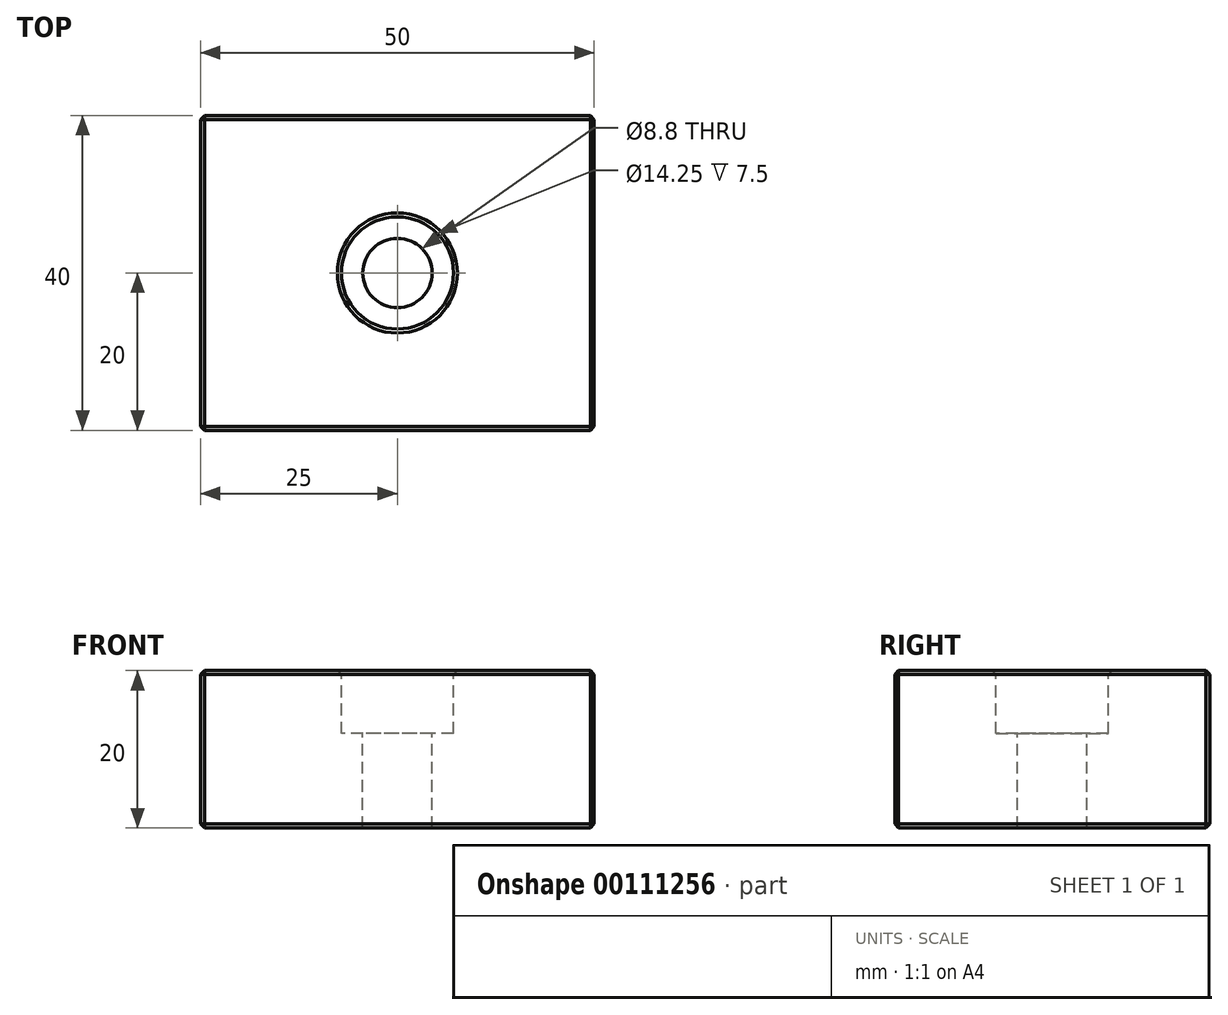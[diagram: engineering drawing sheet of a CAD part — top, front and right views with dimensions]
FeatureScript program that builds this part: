
annotation { "Feature Type Name" : "Feature", "Feature Type Description" : "" }
export const myFeature = defineFeature(function(context is Context, id is Id, definition is map)
    precondition{}
    {
        {
            var Q0;
            Q0=qCreatedBy(makeId("Top.planeOp"),FACE);
            var sketch = newSketch(context, id + "F0", { "sketchPlane" : qUnion([Q0])});
            skLineSegment(sketch, "E0.bottom", {"start": v(25, 20) * mm, "end": v(-25, 20) * mm});
            skLineSegment(sketch, "E0.top", {"start": v(25, -20) * mm, "end": v(-25, -20) * mm});
            skLineSegment(sketch, "E0.left", {"start": v(25, 20) * mm, "end": v(25, -20) * mm});
            skLineSegment(sketch, "E0.right", {"start": v(-25, 20) * mm, "end": v(-25, -20) * mm});
            skPoint(sketch, "E0.middle", {"position": v(0, 0) * mm});
            skSolve(sketch);
        }
        {
            var Q0;
            Q0=makeQuery(id+"F0.imprint","IMPRINT",FACE,{"disambiguationData":[TD([[makeQuery(id+"F0.imprint","IMPRINT",EDGE,{"derivedFrom":sQuery(id+"F0.wireOp",EDGE,"E0.bottom")}),1.0]])]});
            extrude(context, id + "F1", {"entities" : qUnion([Q0]), "depth" : 20 * mm});
        }
        {
            var Q0;
            Q0=makeQuery(id+"F1.opExtrude","CAP_FACE",FACE,{"disambiguationData":[OSD([sQuery(id+"F0.wireOp",EDGE,"E0.bottom"),sQuery(id+"F0.wireOp",EDGE,"E0.top"),sQuery(id+"F0.wireOp",EDGE,"E0.left"),sQuery(id+"F0.wireOp",EDGE,"E0.right")])],"isStart":false});
            var sketch = newSketch(context, id + "F2", { "sketchPlane" : qUnion([Q0])});
            skLineSegment(sketch, "E1", {"start": v(-25, 0) * mm, "end": v(25, 0) * mm});
            skPoint(sketch, "E2", {"position": v(0, 0) * mm});
            skSolve(sketch);
        }
        {
            var Q0;
            Q0=sQuery(id+"F2.wireOp",VERTEX,"E2");
            var Q1;
            Q1=makeQuery(id+"F1.opExtrude","SWEPT_BODY",BODY,{"disambiguationData":[OSD([sQuery(id+"F0.wireOp",EDGE,"E0.bottom"),sQuery(id+"F0.wireOp",EDGE,"E0.top"),sQuery(id+"F0.wireOp",EDGE,"E0.left"),sQuery(id+"F0.wireOp",EDGE,"E0.right")])]});
            hole(context, id + "F3", {"style" : HoleStyle.C_BORE, "endStyle" : HoleEndStyle.THROUGH, "standardTappedOrClearance" : lookupTablePath({ "standard" : "ISO", "fit" : "Normal", "size" : "M8", "type" : "Clearance" }), "standardBlindInLast" : lookupTablePath({ "fit" : "Standard", "standard" : "ISO", "size" : "M8", "type" : "Clearance" }), "holeDiameter" : 8.8 * mm, "cBoreDiameter" : 14.25 * mm, "cBoreDepth" : 8 * mm, "locations" : qUnion([Q0]), "scope" : qUnion([Q1]), "isTappedThrough" : true});
        }
        {
            var Q0;
            Q0=makeQuery(id+"F1.opExtrude","CAP_FACE",FACE,{"disambiguationData":[OSD([sQuery(id+"F0.wireOp",EDGE,"E0.bottom"),sQuery(id+"F0.wireOp",EDGE,"E0.top"),sQuery(id+"F0.wireOp",EDGE,"E0.left"),sQuery(id+"F0.wireOp",EDGE,"E0.right")])],"isStart":false});
            var Q1;
            Q1=makeQuery(id+"F1.opExtrude","SWEPT_FACE",FACE,{"disambiguationData":[OSD([sQuery(id+"F0.wireOp",EDGE,"E0.right")])]});
            var Q2;
            Q2=makeQuery(id+"F1.opExtrude","SWEPT_FACE",FACE,{"disambiguationData":[OSD([sQuery(id+"F0.wireOp",EDGE,"E0.bottom")])]});
            var Q3;
            Q3=makeQuery(id+"F1.opExtrude","SWEPT_FACE",FACE,{"disambiguationData":[OSD([sQuery(id+"F0.wireOp",EDGE,"E0.top")])]});
            var Q4;
            Q4=makeQuery(id+"F1.opExtrude","SWEPT_FACE",FACE,{"disambiguationData":[OSD([sQuery(id+"F0.wireOp",EDGE,"E0.left")])]});
            chamfer(context, id + "F4", {"entities" : qUnion([Q0, Q1, Q2, Q3, Q4]), "width" : 0.5 * mm});
        }
    });
